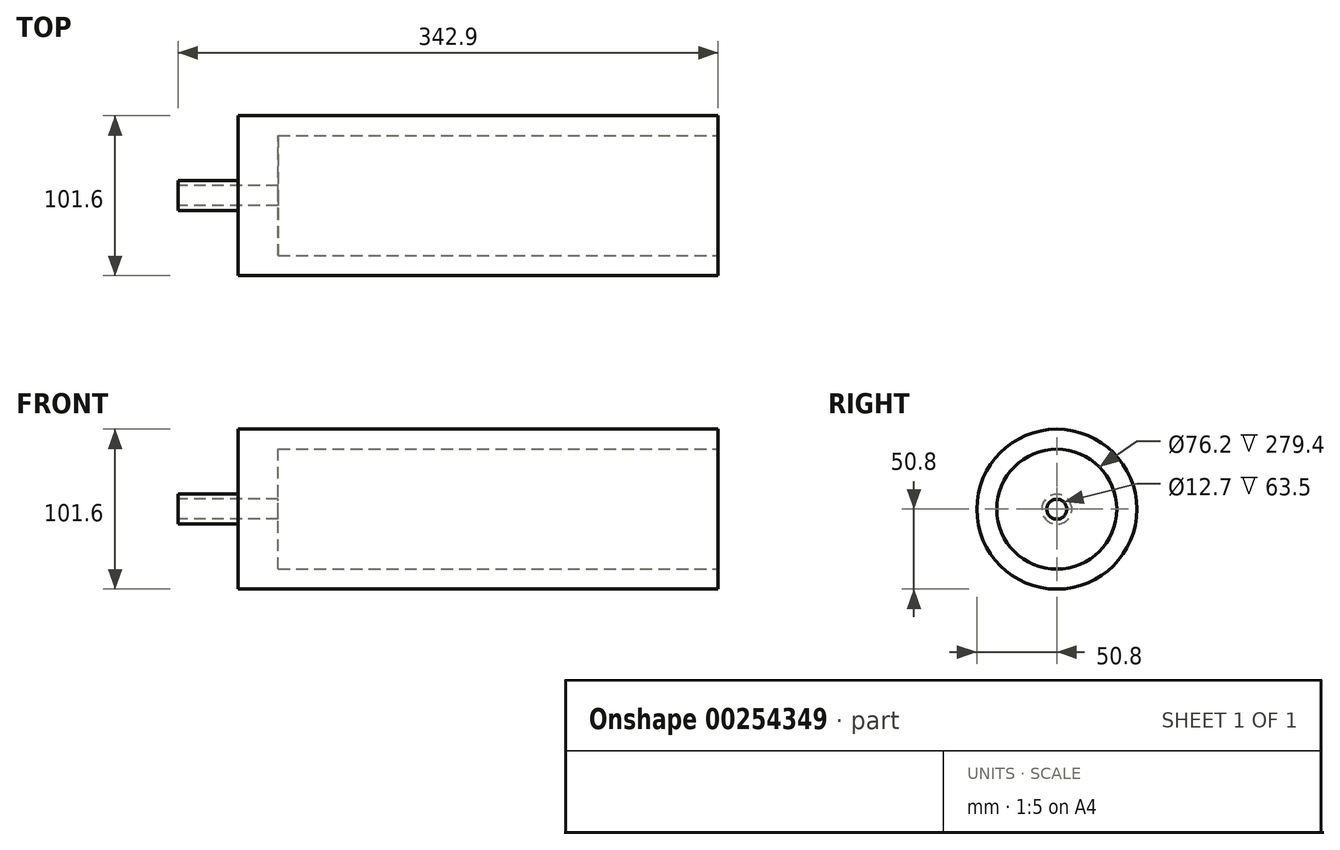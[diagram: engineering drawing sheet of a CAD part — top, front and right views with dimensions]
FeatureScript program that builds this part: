
annotation { "Feature Type Name" : "Feature", "Feature Type Description" : "" }
export const myFeature = defineFeature(function(context is Context, id is Id, definition is map)
    precondition{}
    {
        {
            var Q0;
            Q0=qCreatedBy(makeId("Right.planeOp"),FACE);
            var sketch = newSketch(context, id + "F0", { "sketchPlane" : qUnion([Q0])});
            skCircle(sketch, "E0", {"center": v(0, 0) * mm, "radius": 50.8 * mm});
            skSolve(sketch);
        }
        {
            var Q0;
            Q0 = qSketchRegion(id + "F0", true);
            extrude(context, id + "F1", {"entities" : qUnion([Q0]), "depth" : 304.8 * mm});
        }
        {
            var Q0;
            Q0=makeQuery(id+"F1.opExtrude","CAP_FACE",FACE,{"disambiguationData":[OSD([sQuery(id+"F0.wireOp",EDGE,"E0")])],"isStart":false});
            var sketch = newSketch(context, id + "F2", { "sketchPlane" : qUnion([Q0])});
            skCircle(sketch, "E1", {"center": v(0, 0) * mm, "radius": 38.1 * mm});
            skSolve(sketch);
        }
        {
            var Q0;
            Q0=makeQuery(id+"F2.imprint","IMPRINT",FACE,{"disambiguationData":[TD([[makeQuery(id+"F2.imprint","IMPRINT",EDGE,{"derivedFrom":sQuery(id+"F2.wireOp",EDGE,"E1")}),1.0]])]});
            extrude(context, id + "F3", {"entities" : qUnion([Q0]), "operationType" : NewBodyOperationType.REMOVE, "oppositeDirection" : true, "depth" : 279.4 * mm});
        }
        {
            var Q0;
            Q0=makeQuery(id+"F1.opExtrude","CAP_FACE",FACE,{"disambiguationData":[OSD([sQuery(id+"F0.wireOp",EDGE,"E0")])],"isStart":true});
            var sketch = newSketch(context, id + "F4", { "sketchPlane" : qUnion([Q0])});
            skCircle(sketch, "E2", {"center": v(0, 0) * mm, "radius": 9.53 * mm});
            skSolve(sketch);
        }
        {
            var Q0;
            Q0 = qSketchRegion(id + "F4", true);
            extrude(context, id + "F5", {"entities" : qUnion([Q0]), "operationType" : NewBodyOperationType.ADD, "depth" : 38.1 * mm});
        }
        {
            var Q0;
            Q0=makeQuery(id+"F5.opExtrude","CAP_FACE",FACE,{"disambiguationData":[OSD([sQuery(id+"F4.wireOp",EDGE,"E2")])],"isStart":false});
            var sketch = newSketch(context, id + "F6", { "sketchPlane" : qUnion([Q0])});
            skCircle(sketch, "E3", {"center": v(0, 0) * mm, "radius": 6.35 * mm});
            skSolve(sketch);
        }
        {
            var Q0;
            Q0=makeQuery(id+"F6.imprint","IMPRINT",FACE,{"disambiguationData":[TD([[makeQuery(id+"F6.imprint","IMPRINT",EDGE,{"derivedFrom":sQuery(id+"F6.wireOp",EDGE,"E3")}),1.0]])]});
            extrude(context, id + "F7", {"entities" : qUnion([Q0]), "operationType" : NewBodyOperationType.REMOVE, "oppositeDirection" : true, "depth" : 91.95 * mm});
        }
    });
